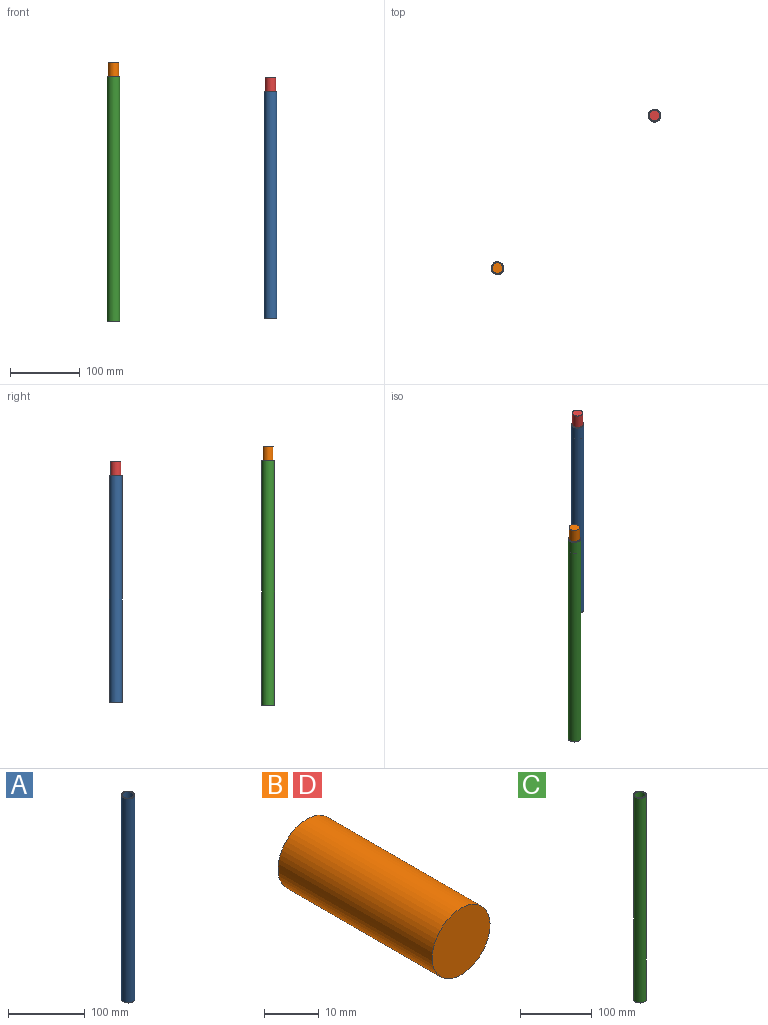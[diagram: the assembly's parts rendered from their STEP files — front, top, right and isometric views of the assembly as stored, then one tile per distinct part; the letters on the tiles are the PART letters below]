
ASSEMBLY  parts=4 mates=2
PART A: 4 faces, bbox 18x18x325 mm
  f0: plane 18x18mm, normal (0,0,-1), area 77.8mm2, adj f2,f3
  f1: plane 18x18mm, normal (0,0,1), area 77.8mm2, adj f2,f3
  f2: cylinder r=9mm len=325mm, axis (0,0,1), area 18378.3mm2, adj f0,f1
  f3: cylinder r=7.5mm len=325mm, axis (0,0,1), area 15315.3mm2, adj f0,f1
PART B: 3 faces, bbox 15x40x15 mm
  f0: cylinder r=7.5mm len=40mm, axis (0,1,0), area 1885mm2, adj f1,f2
  f1: plane 15x15mm, normal (0,-1,0), area 176.7mm2, adj f0
  f2: plane 15x15mm, normal (0,1,0), area 176.7mm2, adj f0
PART C: 4 faces, bbox 18x18x350 mm
  f0: plane 18x18mm, normal (0,0,-1), area 77.8mm2, adj f2,f3
  f1: plane 18x18mm, normal (0,0,1), area 77.8mm2, adj f2,f3
  f2: cylinder r=9mm len=350mm, axis (0,0,1), area 19792mm2, adj f0,f1
  f3: cylinder r=7.5mm len=350mm, axis (0,0,1), area 16493.4mm2, adj f0,f1
PART D: same geometry as B
PLACE A t=(70.23,68.26,8.48)mm
PLACE B rot(axis=(1,0,0),90deg) t=(-154.6,-150.07,374.54)mm
PLACE C t=(-154.6,-150.07,4.54)mm
PLACE D rot(axis=(1,0,0),90deg) t=(70.23,68.26,353.48)mm
MATE fastened B.f0 <-> C.f2  axis (0,0,1) through (-154.6,-150.07,354.54)mm
MATE fastened D.f0 <-> A.f2  axis (0,0,1) through (70.23,68.26,333.48)mm
